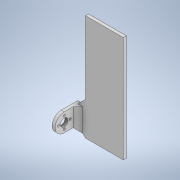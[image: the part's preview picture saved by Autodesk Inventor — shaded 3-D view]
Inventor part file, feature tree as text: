
AUTODESK INVENTOR PART (.ipt)
format: ipt  version: 2020 (Build 240168000, 168)  size: 206,336 bytes
history: native  units: in
note: dims shown in document units (in); Inventor stores cm internally (conversion verified against a paired STEP export)
features: sketch x6, extrude x5, chamfer x3
ambient origin geometry x8: Origin, YZ Plane, XZ Plane, XY Plane, X Axis, Y Axis, Z Axis, Center Point
bodies: Solid1 (feature_tree)
feature tree (14):
  extrude  "Extrusion1"  Depth=1.2in
  extrude  "Extrusion3"  Depth=0.1406in
  extrude  "Extrusion4"  Depth=0.1406in
  extrude  "Extrusion5"  Depth=0.2in TaperAngle=0.0deg
  chamfer  "Chamfer1"  Distance=0.2in
  chamfer  "Chamfer2"  Distance=0.2in
  chamfer  "Chamfer3"  Distance=0.5in
  extrude  "Extrusion6"  Depth=2.5in
  sketch  "Sketch10"  dims[d18=1.2in d19=0.2in d20=0.0in d21=0.2in d22=0.5in d23=0.0in d24=2.5in d25=6.5in d26=0.5in d27=0.2in d28=0.0in d30=0.3125in d31=0.125in d32=45.0deg d33=0.5in d34=0.125in d35=45.0deg d36=0.5in d37=0.125in d38=45.0deg d47=0.25in d48=6.7in d49=0.25in d50=0.25in d51=0.5in d52=0.5in d53=0.1in d54=0.0in]
  sketch  "Sketch1"  dims[d0=1.2in d1=0.77in]
  sketch  "Sketch5"  dims[d2=0.1406in d3=0.1406in]
  sketch  "Sketch6"  dims[d4=0.1406in d5=0.1406in]
  sketch  "Sketch7"  dims[d6=0.5in d7=0.2in d8=0.0in]
  sketch  "Sketch9"  dims[d17=1.1in]
